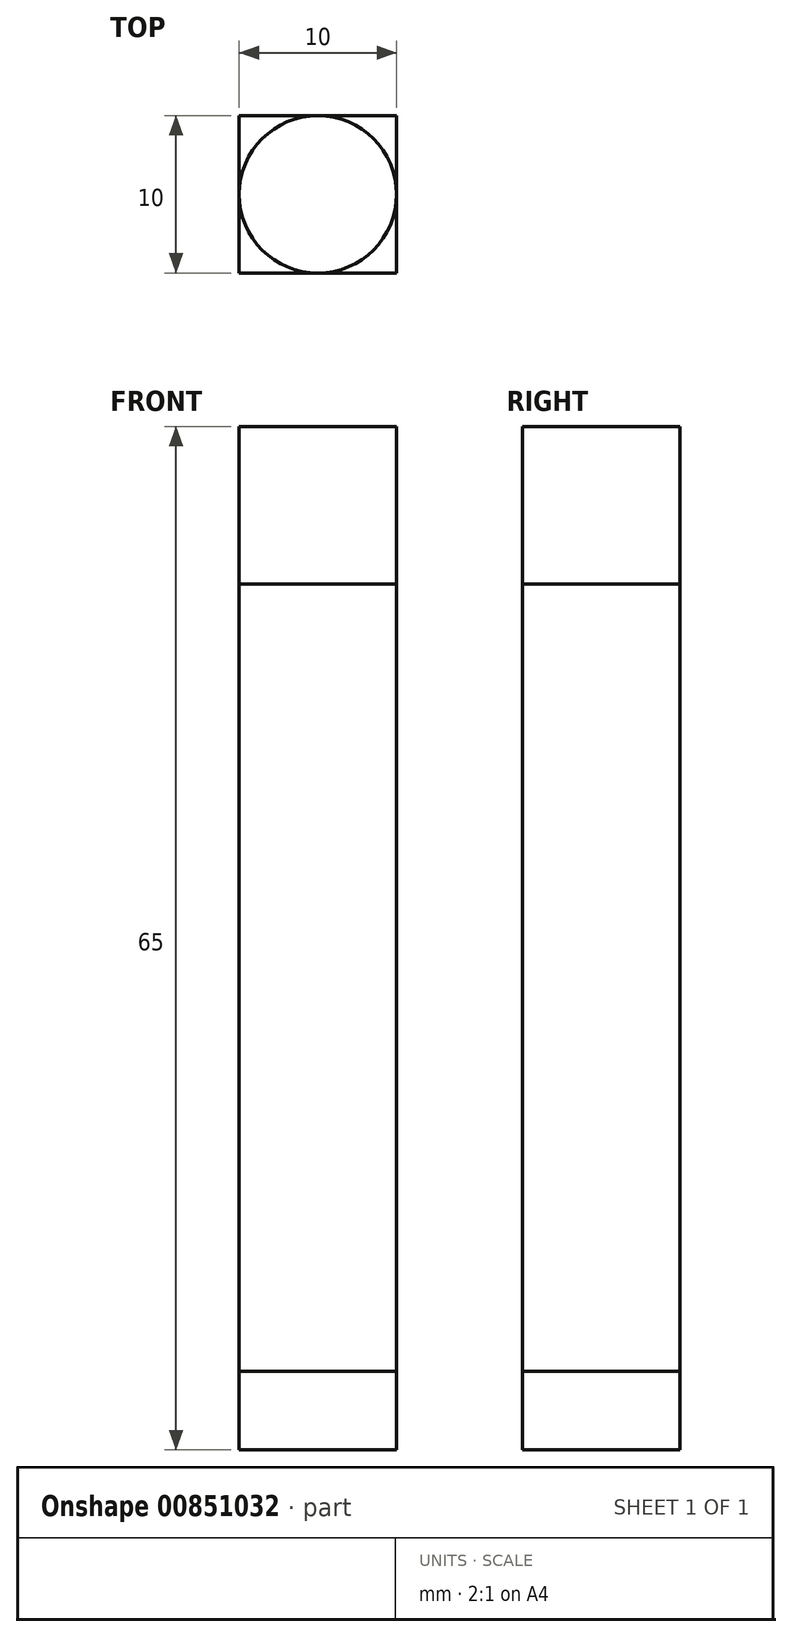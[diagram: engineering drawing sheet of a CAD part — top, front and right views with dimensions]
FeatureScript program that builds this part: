
annotation { "Feature Type Name" : "Feature", "Feature Type Description" : "" }
export const myFeature = defineFeature(function(context is Context, id is Id, definition is map)
    precondition{}
    {
        {
            var Q0;
            Q0=qCreatedBy(makeId("Top.planeOp"),FACE);
            var sketch = newSketch(context, id + "F0", { "sketchPlane" : qUnion([Q0])});
            skLineSegment(sketch, "E0.bottom", {"start": v(5, -5) * mm, "end": v(-5, -5) * mm});
            skLineSegment(sketch, "E0.top", {"start": v(5, 5) * mm, "end": v(-5, 5) * mm});
            skLineSegment(sketch, "E0.left", {"start": v(5, -5) * mm, "end": v(5, 5) * mm});
            skLineSegment(sketch, "E0.right", {"start": v(-5, -5) * mm, "end": v(-5, 5) * mm});
            skPoint(sketch, "E0.middle", {"position": v(0, 0) * mm});
            skSolve(sketch);
        }
        {
            var Q0;
            Q0=makeQuery(id+"F0.imprint","IMPRINT",FACE,{"disambiguationData":[TD([[makeQuery(id+"F0.imprint","IMPRINT",EDGE,{"derivedFrom":sQuery(id+"F0.wireOp",EDGE,"E0.bottom")}),-1.0]])]});
            extrude(context, id + "F1", {"entities" : qUnion([Q0]), "endBound" : BoundingType.SYMMETRIC, "depth" : 50 * mm, "offsetDistance" : 25 * mm});
        }
        {
            var Q0;
            Q0=makeQuery(id+"F1.opExtrude","CAP_FACE",FACE,{"disambiguationData":[OSD([sQuery(id+"F0.wireOp",EDGE,"E0.bottom"),sQuery(id+"F0.wireOp",EDGE,"E0.top"),sQuery(id+"F0.wireOp",EDGE,"E0.left"),sQuery(id+"F0.wireOp",EDGE,"E0.right")])],"isStart":true});
            var sketch = newSketch(context, id + "F2", { "sketchPlane" : qUnion([Q0])});
            skCircle(sketch, "E1", {"center": v(0, 0) * mm, "radius": 5 * mm});
            skSolve(sketch);
        }
        {
            var Q0;
            {var subQ0=sQuery(id+"F2.wireOp",EDGE,"E1");var subQ1=makeQuery(id+"F2.imprint","INTERSECT",VERTEX,{"derivedFrom":[makeQuery(id+"F1.opExtrude","CAP_EDGE",EDGE,{"disambiguationData":[OSD([sQuery(id+"F0.wireOp",EDGE,"E0.bottom")])],"isStart":true}),subQ0]});Q0=makeQuery(id+"F2.imprint","IMPRINT",FACE,{"disambiguationData":[TD([[makeQuery(id+"F2.imprint","IMPRINT",EDGE,{"disambiguationData":[TD([[subQ1,1.0]])],"derivedFrom":subQ0}),1.0]])]});}
            extrude(context, id + "F3", {"entities" : qUnion([Q0]), "operationType" : NewBodyOperationType.ADD, "depth" : 5 * mm, "offsetDistance" : 25 * mm});
        }
        {
            var Q0;
            Q0=makeQuery(id+"F1.opExtrude","CAP_FACE",FACE,{"disambiguationData":[OSD([sQuery(id+"F0.wireOp",EDGE,"E0.bottom"),sQuery(id+"F0.wireOp",EDGE,"E0.top"),sQuery(id+"F0.wireOp",EDGE,"E0.left"),sQuery(id+"F0.wireOp",EDGE,"E0.right")])],"isStart":false});
            var sketch = newSketch(context, id + "F4", { "sketchPlane" : qUnion([Q0])});
            skCircle(sketch, "E2", {"center": v(0, 0) * mm, "radius": 5 * mm});
            skSolve(sketch);
        }
        {
            var Q0;
            {var subQ0=sQuery(id+"F4.wireOp",EDGE,"E2");var subQ1=makeQuery(id+"F4.imprint","INTERSECT",VERTEX,{"derivedFrom":[makeQuery(id+"F1.opExtrude","CAP_EDGE",EDGE,{"disambiguationData":[OSD([sQuery(id+"F0.wireOp",EDGE,"E0.top")])],"isStart":false}),subQ0]});Q0=makeQuery(id+"F4.imprint","IMPRINT",FACE,{"disambiguationData":[TD([[makeQuery(id+"F4.imprint","IMPRINT",EDGE,{"disambiguationData":[TD([[subQ1,1.0]])],"derivedFrom":subQ0}),1.0]])]});}
            extrude(context, id + "F5", {"entities" : qUnion([Q0]), "operationType" : NewBodyOperationType.ADD, "depth" : 10 * mm, "offsetDistance" : 25 * mm});
        }
    });
